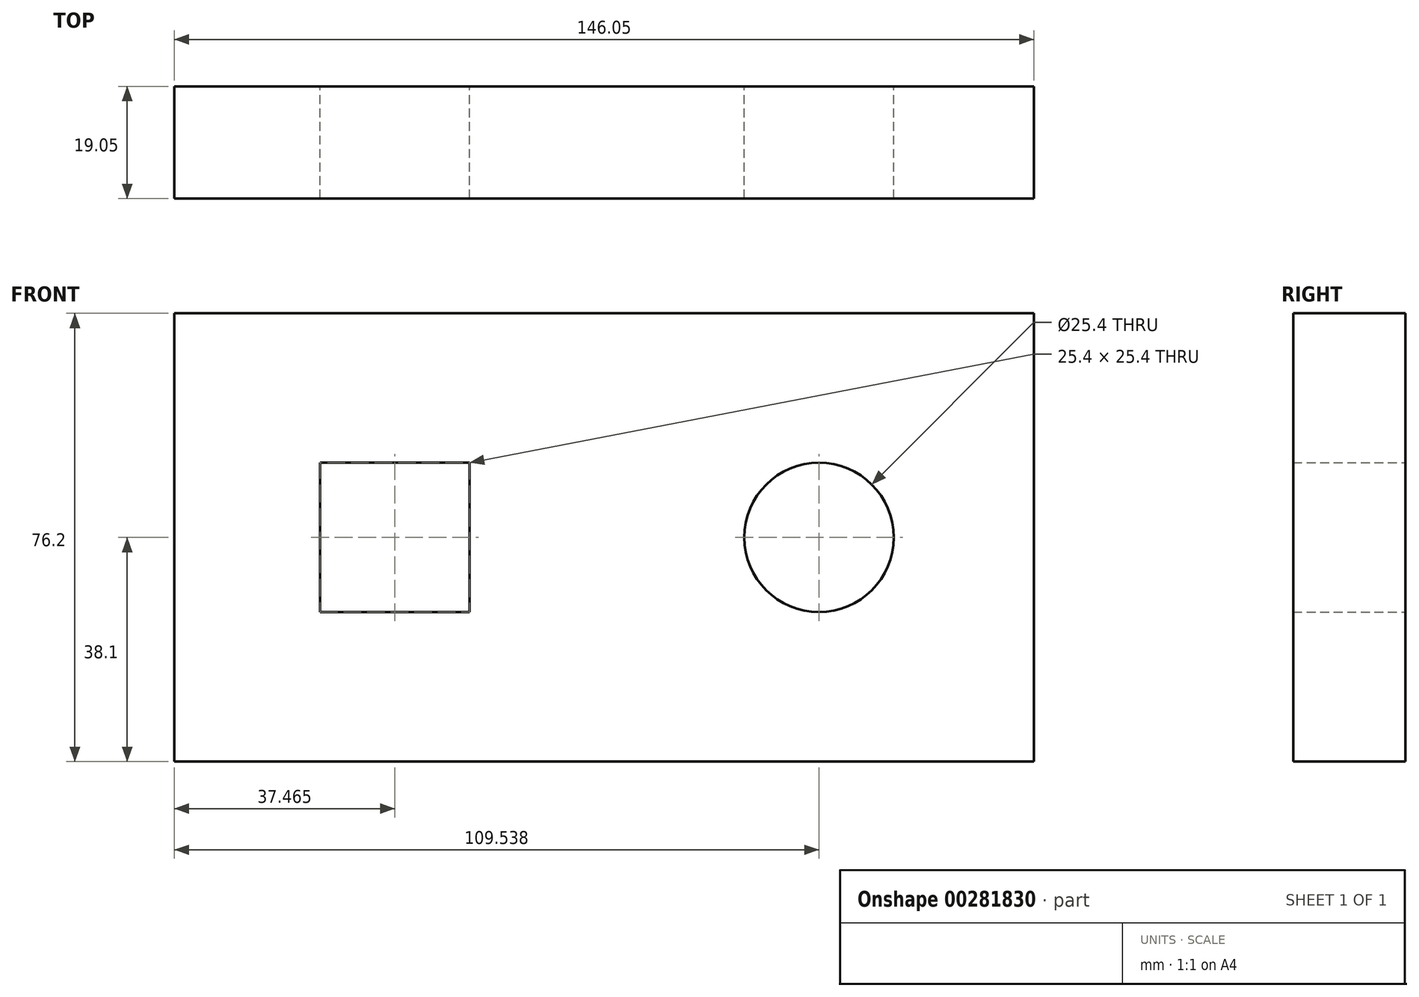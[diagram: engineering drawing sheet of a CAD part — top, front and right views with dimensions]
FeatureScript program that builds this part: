
annotation { "Feature Type Name" : "Feature", "Feature Type Description" : "" }
export const myFeature = defineFeature(function(context is Context, id is Id, definition is map)
    precondition{}
    {
        {
            var Q0;
            Q0=qCreatedBy(makeId("Front.planeOp"),FACE);
            var sketch = newSketch(context, id + "F0", { "sketchPlane" : qUnion([Q0])});
            skLineSegment(sketch, "E0", {"start": v(0, 0) * mm, "end": v(0, 76.2) * mm});
            skLineSegment(sketch, "E1", {"start": v(0, 76.2) * mm, "end": v(-146.05, 76.2) * mm});
            skLineSegment(sketch, "E2", {"start": v(-146.05, 76.2) * mm, "end": v(-146.05, 0) * mm});
            skLineSegment(sketch, "E3", {"start": v(-146.05, 0) * mm, "end": v(0, 0) * mm});
            skCircle(sketch, "E4", {"center": v(-36.51, 38.1) * mm, "radius": 12.7 * mm});
            skLineSegment(sketch, "E5.bottom", {"start": v(-121.29, 50.8) * mm, "end": v(-95.88, 50.8) * mm});
            skLineSegment(sketch, "E5.top", {"start": v(-121.29, 25.4) * mm, "end": v(-95.88, 25.4) * mm});
            skLineSegment(sketch, "E5.left", {"start": v(-121.29, 50.8) * mm, "end": v(-121.29, 25.4) * mm});
            skLineSegment(sketch, "E5.right", {"start": v(-95.88, 50.8) * mm, "end": v(-95.88, 25.4) * mm});
            skSolve(sketch);
        }
        {
            var Q0;
            Q0=makeQuery(id+"F0.imprint","IMPRINT",FACE,{"disambiguationData":[TD([[makeQuery(id+"F0.imprint","IMPRINT",EDGE,{"derivedFrom":sQuery(id+"F0.wireOp",EDGE,"E0")}),1.0]])]});
            extrude(context, id + "F1", {"entities" : qUnion([Q0]), "depth" : 19.05 * mm});
        }
    });
